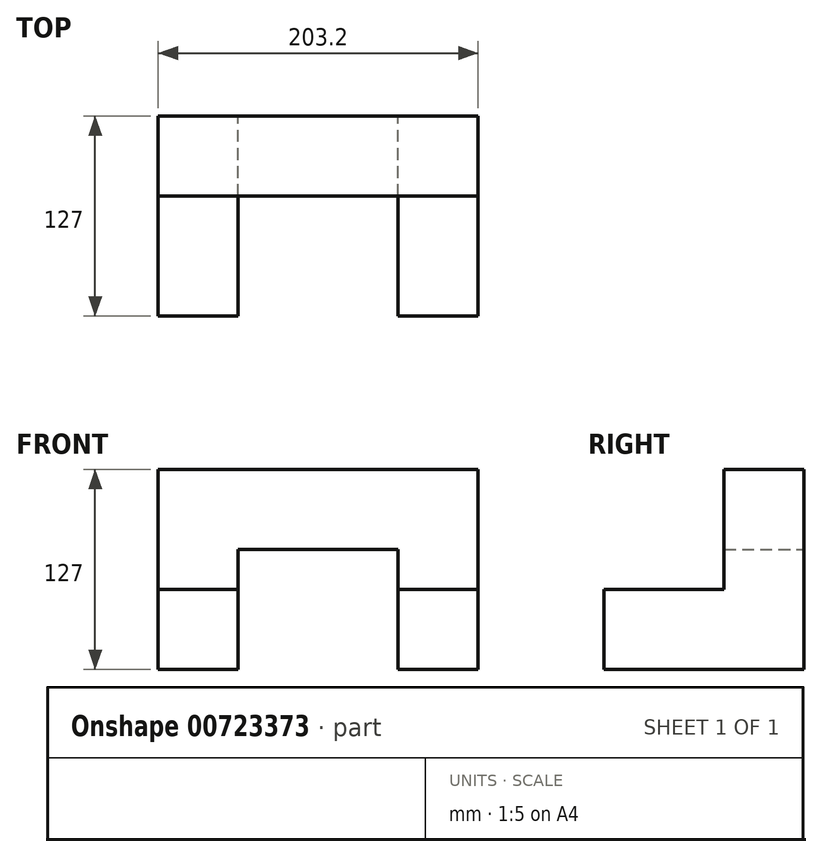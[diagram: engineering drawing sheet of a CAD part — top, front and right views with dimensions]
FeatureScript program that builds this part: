
annotation { "Feature Type Name" : "Feature", "Feature Type Description" : "" }
export const myFeature = defineFeature(function(context is Context, id is Id, definition is map)
    precondition{}
    {
        {
            var Q0;
            Q0=qCreatedBy(makeId("Front.planeOp"),FACE);
            var sketch = newSketch(context, id + "F0", { "sketchPlane" : qUnion([Q0])});
            skLineSegment(sketch, "E0", {"start": v(-72.27, -47.16) * mm, "end": v(-72.27, 79.84) * mm});
            skLineSegment(sketch, "E1", {"start": v(-72.27, 79.84) * mm, "end": v(130.93, 79.84) * mm});
            skLineSegment(sketch, "E2", {"start": v(130.93, 79.84) * mm, "end": v(130.93, -47.16) * mm});
            skLineSegment(sketch, "E3", {"start": v(130.93, -47.16) * mm, "end": v(80.13, -47.16) * mm});
            skLineSegment(sketch, "E4", {"start": v(80.13, -47.16) * mm, "end": v(80.13, 29.04) * mm});
            skLineSegment(sketch, "E5", {"start": v(80.13, 29.04) * mm, "end": v(-21.47, 29.04) * mm});
            skLineSegment(sketch, "E6", {"start": v(-21.47, 29.04) * mm, "end": v(-21.47, -47.16) * mm});
            skLineSegment(sketch, "E7", {"start": v(-21.47, -47.16) * mm, "end": v(-72.27, -47.16) * mm});
            skSolve(sketch);
        }
        {
            var Q0;
            Q0=makeQuery(id+"F0.imprint","IMPRINT",FACE,{"disambiguationData":[TD([[makeQuery(id+"F0.imprint","IMPRINT",EDGE,{"derivedFrom":sQuery(id+"F0.wireOp",EDGE,"E0")}),-1.0]])]});
            extrude(context, id + "F1", {"entities" : qUnion([Q0]), "depth" : 50.8 * mm, "offsetDistance" : 25.4 * mm});
        }
        {
            var Q0;
            Q0=makeQuery(id+"F1.opExtrude","CAP_FACE",FACE,{"disambiguationData":[OSD([sQuery(id+"F0.wireOp",EDGE,"E0"),sQuery(id+"F0.wireOp",EDGE,"E1"),sQuery(id+"F0.wireOp",EDGE,"E2"),sQuery(id+"F0.wireOp",EDGE,"E3"),sQuery(id+"F0.wireOp",EDGE,"E4"),sQuery(id+"F0.wireOp",EDGE,"E5"),sQuery(id+"F0.wireOp",EDGE,"E6"),sQuery(id+"F0.wireOp",EDGE,"E7")])],"isStart":false});
            var sketch = newSketch(context, id + "F2", { "sketchPlane" : qUnion([Q0])});
            skLineSegment(sketch, "E8", {"start": v(-72.27, -47.16) * mm, "end": v(-72.27, 3.64) * mm});
            skLineSegment(sketch, "E9", {"start": v(-72.27, 3.64) * mm, "end": v(-21.47, 3.64) * mm});
            skLineSegment(sketch, "E10", {"start": v(-21.47, 3.64) * mm, "end": v(-21.47, -47.16) * mm});
            skLineSegment(sketch, "E11", {"start": v(-21.47, -47.16) * mm, "end": v(-72.27, -47.16) * mm});
            skSolve(sketch);
        }
        {
            var Q0;
            Q0=makeQuery(id+"F2.imprint","IMPRINT",FACE,{"disambiguationData":[TD([[makeQuery(id+"F2.imprint","IMPRINT",EDGE,{"derivedFrom":sQuery(id+"F2.wireOp",EDGE,"E8")}),-1.0]])]});
            extrude(context, id + "F3", {"entities" : qUnion([Q0]), "operationType" : NewBodyOperationType.ADD, "depth" : 76.2 * mm, "offsetDistance" : 25.4 * mm});
        }
        {
            var Q0;
            Q0=makeQuery(id+"F1.opExtrude","CAP_FACE",FACE,{"disambiguationData":[OSD([sQuery(id+"F0.wireOp",EDGE,"E0"),sQuery(id+"F0.wireOp",EDGE,"E1"),sQuery(id+"F0.wireOp",EDGE,"E2"),sQuery(id+"F0.wireOp",EDGE,"E3"),sQuery(id+"F0.wireOp",EDGE,"E4"),sQuery(id+"F0.wireOp",EDGE,"E5"),sQuery(id+"F0.wireOp",EDGE,"E6"),sQuery(id+"F0.wireOp",EDGE,"E7")])],"isStart":false});
            var sketch = newSketch(context, id + "F4", { "sketchPlane" : qUnion([Q0])});
            skLineSegment(sketch, "E12", {"start": v(80.13, -47.16) * mm, "end": v(80.13, 3.64) * mm});
            skLineSegment(sketch, "E13", {"start": v(80.13, 3.64) * mm, "end": v(130.93, 3.64) * mm});
            skLineSegment(sketch, "E14", {"start": v(130.93, 3.64) * mm, "end": v(130.93, -47.16) * mm});
            skLineSegment(sketch, "E15", {"start": v(130.93, -47.16) * mm, "end": v(80.13, -47.16) * mm});
            skSolve(sketch);
        }
        {
            var Q0;
            Q0=makeQuery(id+"F4.imprint","IMPRINT",FACE,{"disambiguationData":[TD([[makeQuery(id+"F4.imprint","IMPRINT",EDGE,{"derivedFrom":sQuery(id+"F4.wireOp",EDGE,"E12")}),-1.0]])]});
            extrude(context, id + "F5", {"entities" : qUnion([Q0]), "operationType" : NewBodyOperationType.ADD, "depth" : 76.2 * mm, "offsetDistance" : 25.4 * mm});
        }
    });
